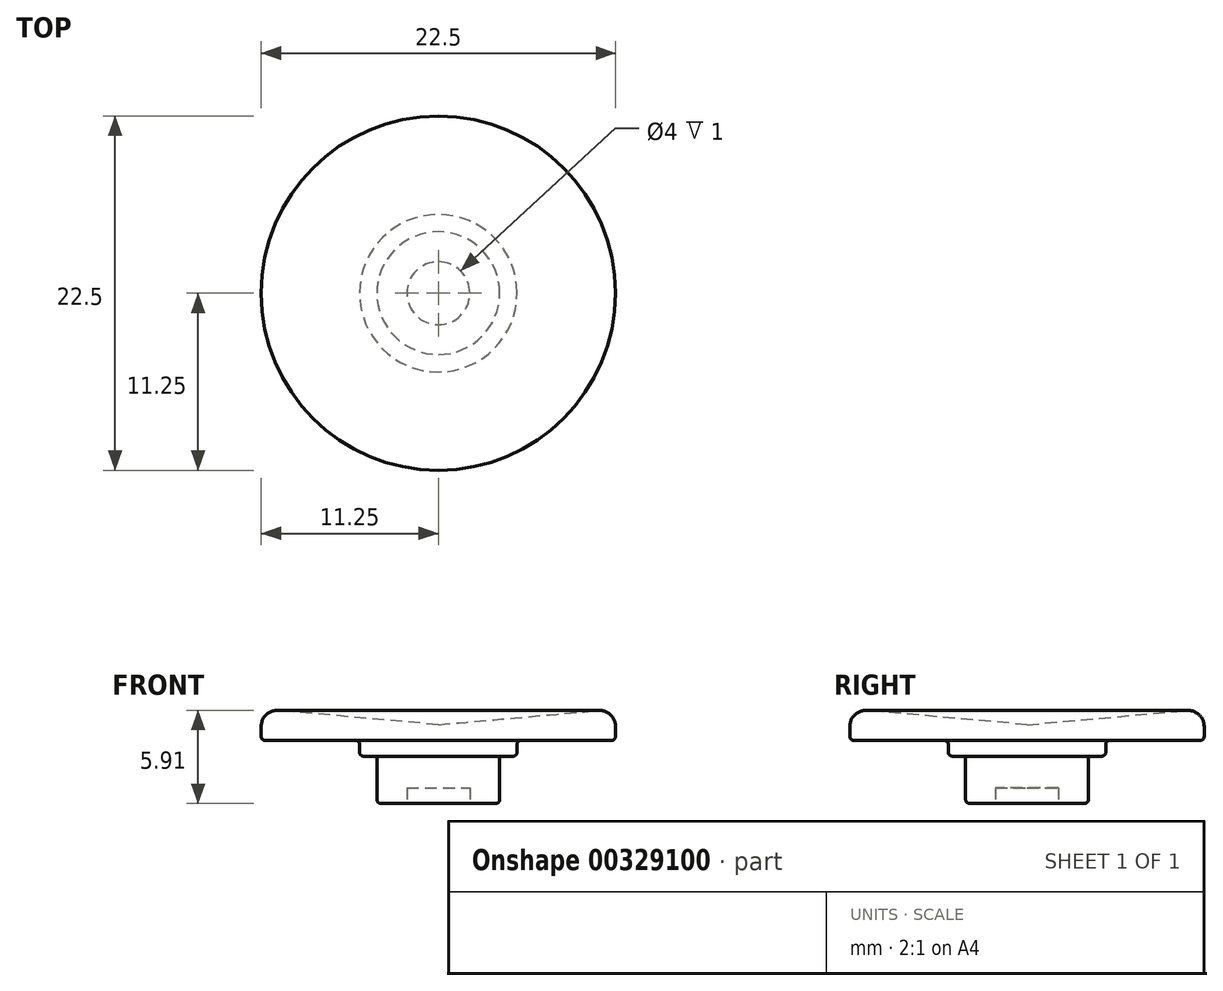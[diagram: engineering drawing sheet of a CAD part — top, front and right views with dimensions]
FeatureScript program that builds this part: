
annotation { "Feature Type Name" : "Feature", "Feature Type Description" : "" }
export const myFeature = defineFeature(function(context is Context, id is Id, definition is map)
    precondition{}
    {
        {
            var Q0;
            Q0=qCreatedBy(makeId("Top.planeOp"),FACE);
            var sketch = newSketch(context, id + "F0", { "sketchPlane" : qUnion([Q0])});
            skCircle(sketch, "E0", {"center": v(0, 0) * mm, "radius": 3.9 * mm});
            skCircle(sketch, "E1", {"center": v(0, 0) * mm, "radius": 5 * mm});
            skCircle(sketch, "E2", {"center": v(0, 0) * mm, "radius": 11.25 * mm, "construction": true});
            skSolve(sketch);
        }
        {
            var Q0;
            Q0=makeQuery(id+"F0.imprint","IMPRINT",FACE,{"disambiguationData":[TD([[makeQuery(id+"F0.imprint","IMPRINT",EDGE,{"derivedFrom":sQuery(id+"F0.wireOp",EDGE,"E0")}),1.0]])]});
            extrude(context, id + "F1", {"entities" : qUnion([Q0]), "oppositeDirection" : true, "depth" : 3 * mm});
        }
        {
            var Q0;
            Q0=makeQuery(id+"F0.imprint","IMPRINT",FACE,{"disambiguationData":[TD([[makeQuery(id+"F0.imprint","IMPRINT",EDGE,{"derivedFrom":sQuery(id+"F0.wireOp",EDGE,"E0")}),1.0]])]});
            var Q1;
            Q1=makeQuery(id+"F0.imprint","IMPRINT",FACE,{"disambiguationData":[TD([[makeQuery(id+"F0.imprint","IMPRINT",EDGE,{"derivedFrom":sQuery(id+"F0.wireOp",EDGE,"E0")}),-1.0]])]});
            extrude(context, id + "F2", {"entities" : qUnion([Q0, Q1]), "operationType" : NewBodyOperationType.ADD, "depth" : 1 * mm});
        }
        {
            var Q0;
            Q0=makeQuery(id+"F2.opExtrude","CAP_FACE",FACE,{"disambiguationData":[OSD([sQuery(id+"F0.wireOp",EDGE,"E1")])],"isStart":false});
            var sketch = newSketch(context, id + "F3", { "sketchPlane" : qUnion([Q0])});
            skCircle(sketch, "E3.0", {"center": v(0, 0) * mm, "radius": 11.25 * mm});
            skSolve(sketch);
        }
        {
            var Q0;
            Q0 = qSketchRegion(id + "F3", true);
            extrude(context, id + "F4", {"entities" : qUnion([Q0]), "operationType" : NewBodyOperationType.ADD, "depth" : 2 * mm});
        }
        {
            var Q0;
            Q0=qCreatedBy(makeId("Front.planeOp"),FACE);
            var sketch = newSketch(context, id + "F5", { "sketchPlane" : qUnion([Q0])});
            skLineSegment(sketch, "E4", {"start": v(11.25, 3) * mm, "end": v(0, 3) * mm});
            skLineSegment(sketch, "E5", {"start": v(0, 3) * mm, "end": v(0, 2) * mm});
            skLineSegment(sketch, "E6", {"start": v(0, 0) * mm, "end": v(0, 2) * mm, "construction": true});
            skLineSegment(sketch, "E7", {"start": v(0, 2) * mm, "end": v(11.25, 3) * mm});
            skSolve(sketch);
        }
        {
            var Q0;
            Q0 = qSketchRegion(id + "F5", true);
            var Q1;
            Q1=sQuery(id+"F5.wireOp",EDGE,"E6");
            revolve(context, id + "F6", {"operationType" : NewBodyOperationType.REMOVE, "entities" : qUnion([Q0]), "axis" : qUnion([Q1]), "revolveType" : RevolveType.FULL, "oppositeDirection" : true});
        }
        {
            var Q0;
            Q0=makeQuery(id+"F6.boolean.opBoolean","MERGE",EDGE,{"derivedFrom":[makeQuery(id+"F4.opExtrude","CAP_EDGE",EDGE,{"disambiguationData":[OSD([sQuery(id+"F3.wireOp",EDGE,"E3.0")])],"isStart":false}),makeQuery(id+"F6.opRevolve","SWEPT_EDGE",EDGE,{"disambiguationData":[OSD([sQuery(id+"F5.wireOp",EDGE,"E4"),sQuery(id+"F5.wireOp",EDGE,"E7")])]})]});
            fillet(context, id + "F7", {"entities" : qUnion([Q0]), "radius" : 1 * mm, "tangentPropagation" : true, "allowEdgeOverflow" : false});
        }
        {
            var Q0;
            Q0=makeQuery(id+"F1.opExtrude","CAP_FACE",FACE,{"disambiguationData":[OSD([sQuery(id+"F0.wireOp",EDGE,"E0")])],"isStart":false});
            var sketch = newSketch(context, id + "F8", { "sketchPlane" : qUnion([Q0])});
            skCircle(sketch, "E8", {"center": v(0, 0) * mm, "radius": 2 * mm});
            skSolve(sketch);
        }
        {
            var Q0;
            Q0 = qSketchRegion(id + "F8", true);
            extrude(context, id + "F9", {"entities" : qUnion([Q0]), "operationType" : NewBodyOperationType.REMOVE, "oppositeDirection" : true, "depth" : 1 * mm});
        }
        {
            var Q0;
            Q0=makeQuery(id+"F1.opExtrude","CAP_EDGE",EDGE,{"disambiguationData":[OSD([sQuery(id+"F0.wireOp",EDGE,"E0")])],"isStart":false});
            fillet(context, id + "F10", {"entities" : qUnion([Q0]), "radius" : 0.25 * mm, "tangentPropagation" : true, "allowEdgeOverflow" : false});
        }
        {
            var Q0;
            Q0=makeQuery(id+"F2.opExtrude","CAP_EDGE",EDGE,{"disambiguationData":[OSD([sQuery(id+"F0.wireOp",EDGE,"E1")])],"isStart":true});
            fillet(context, id + "F11", {"entities" : qUnion([Q0]), "radius" : 0.25 * mm, "tangentPropagation" : true, "allowEdgeOverflow" : false});
        }
        {
            var Q0;
            Q0=makeQuery(id+"F1.opExtrude","CAP_EDGE",EDGE,{"disambiguationData":[OSD([sQuery(id+"F0.wireOp",EDGE,"E0")])],"isStart":true});
            var Q1;
            Q1=makeQuery(id+"F4.opExtrude","CAP_FACE",FACE,{"disambiguationData":[OSD([sQuery(id+"F3.wireOp",EDGE,"E3.0")])],"isStart":true});
            fillet(context, id + "F12", {"entities" : qUnion([Q0, Q1]), "radius" : 0.25 * mm, "tangentPropagation" : true, "allowEdgeOverflow" : false});
        }
    });
